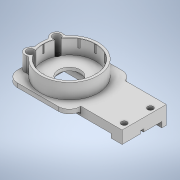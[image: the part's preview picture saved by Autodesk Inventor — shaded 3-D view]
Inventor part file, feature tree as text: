
AUTODESK INVENTOR PART (.ipt)
format: ipt  version: 2022 (Build 260153000, 153)  size: 530,432 bytes
history: native  units: mm
features: extrude x13, sketch x13, fillet x5, other x3, mirror x1, pattern_circular x1
ambient origin geometry x8: Origin, YZ Plane, XZ Plane, XY Plane, X Axis, Y Axis, Z Axis, Center Point
bodies: Body1 (feature_tree)
feature tree (36):
  extrude  "Выдавливание2"  Depth=28.6mm
  sketch  "Эскиз2"
  extrude  "Выдавливание3"  Depth=12.05mm
  extrude  "Выдавливание11"  Depth=31.58mm
  extrude  "Выдавливание12"  Depth=14.05mm
  extrude  "Выдавливание13"  Depth=29.1mm
  extrude  "Выдавливание14"  Depth=75.0mm
  other  "РабПлоскость2"
  mirror  "Зеркальное отражение2"
  extrude  "Выдавливание15"  Depth=3.0mm
  extrude  "Выдавливание18"  Depth=4.0mm TaperAngle=0.0deg
  fillet  "Сопряжение5"  Radius=4.1mm
  extrude  "Выдавливание19"  Depth=19.0mm
  fillet  "Сопряжение6"  Radius=68.0mm
  other  "РабОсь1"
  pattern_circular  "Круговой массив1"  [2 undecoded]
  extrude  "Выдавливание20"  Depth=4.1mm TaperAngle=0.0deg
  extrude  "Выдавливание21"  Depth=22.25mm
  fillet  "Сопряжение8"  Radius=16.0mm
  fillet  "Сопряжение9"  Radius=2.1mm
  other  "РабПлоскость4"
  extrude  "Выдавливание26"  Depth=59.05mm
  fillet  "Сопряжение10"  Radius=28.6mm
  extrude  "Выдавливание27"  Depth=4.475mm
  sketch  "Эскиз1"
  sketch  "Эскиз9"
  sketch  "Эскиз10"
  sketch  "Эскиз11"
  sketch  "Эскиз12"
  sketch  "Эскиз13"
  sketch  "Эскиз15"
  sketch  "Эскиз16"
  sketch  "Эскиз17"
  sketch  "Эскиз18"
  sketch  "Эскиз23"
  sketch  "Эскиз24"
note: 2 required parameter values undecoded (feature->parameter linkage not recoverable at this tier; creation-order binding heuristic only, values carry confidence <= 0.55)
